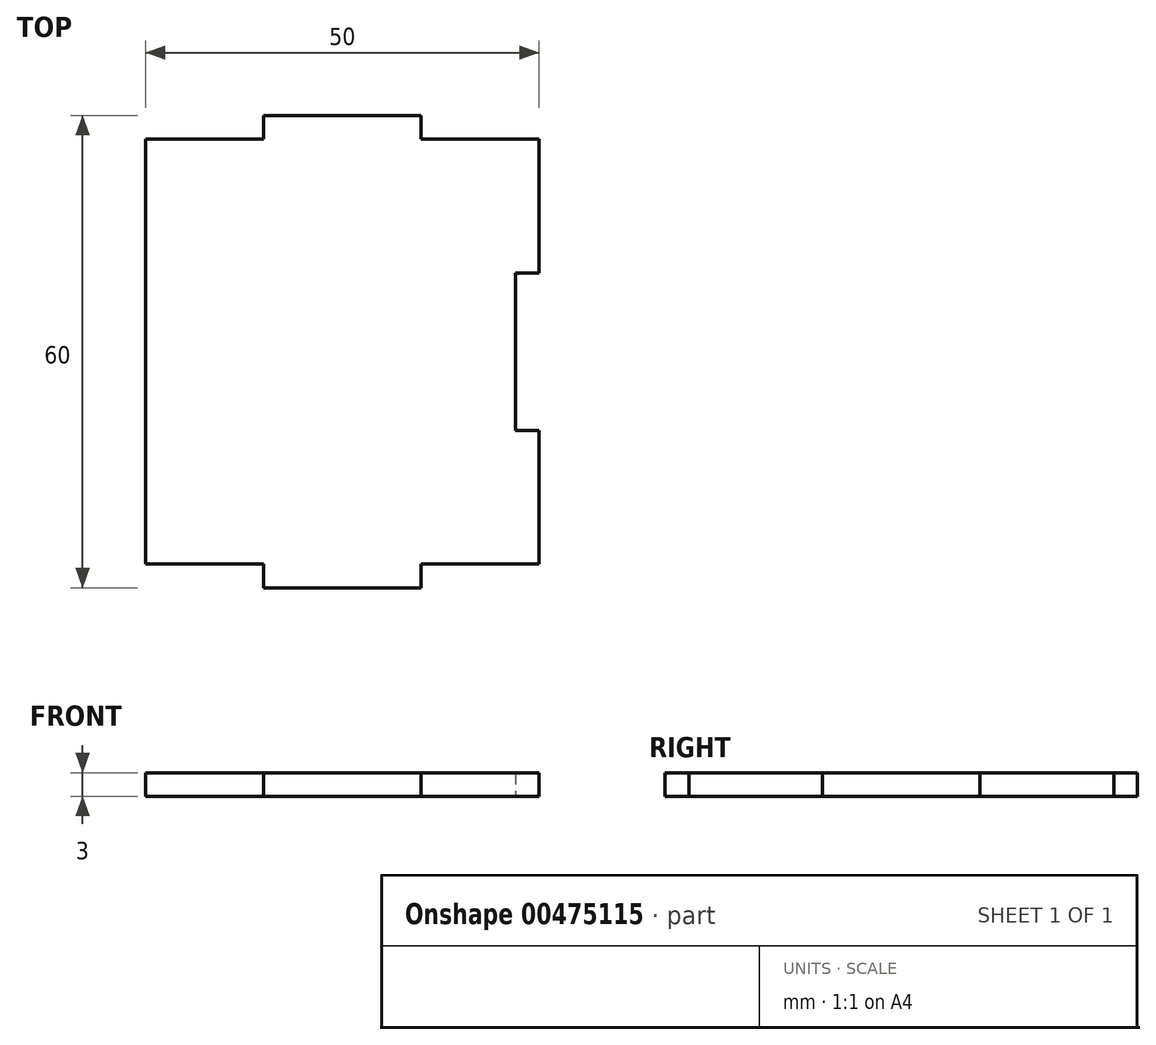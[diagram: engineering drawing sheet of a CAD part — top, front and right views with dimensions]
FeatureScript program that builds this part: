
annotation { "Feature Type Name" : "Feature", "Feature Type Description" : "" }
export const myFeature = defineFeature(function(context is Context, id is Id, definition is map)
    precondition{}
    {
        {
            var Q0;
            Q0=qCreatedBy(makeId("Top.planeOp"),FACE);
            var sketch = newSketch(context, id + "F0", { "sketchPlane" : qUnion([Q0])});
            skLineSegment(sketch, "E0.bottom", {"start": v(10, 30) * mm, "end": v(-10, 30) * mm});
            skLineSegment(sketch, "E0.top", {"start": v(10, -30) * mm, "end": v(-10, -30) * mm});
            skLineSegment(sketch, "E0.left", {"start": v(25, 27) * mm, "end": v(25, 10) * mm});
            skLineSegment(sketch, "E0.right", {"start": v(-25, 27) * mm, "end": v(-25, -27) * mm});
            skPoint(sketch, "E0.middle", {"position": v(0, 0) * mm});
            skLineSegment(sketch, "E1", {"start": v(-10, -30) * mm, "end": v(10, -30) * mm});
            skLineSegment(sketch, "E2", {"start": v(-10, -30) * mm, "end": v(-10, -27) * mm});
            skLineSegment(sketch, "E3", {"start": v(-10, -27) * mm, "end": v(-25, -27) * mm});
            skLineSegment(sketch, "E4", {"start": v(10, -30) * mm, "end": v(10, -27) * mm});
            skLineSegment(sketch, "E5", {"start": v(10, -27) * mm, "end": v(25, -27) * mm});
            skPoint(sketch, "E6.orphan", {"position": v(-25, -30) * mm});
            skPoint(sketch, "E7.orphan", {"position": v(25, -30) * mm});
            skLineSegment(sketch, "E8", {"start": v(-10, 30) * mm, "end": v(10, 30) * mm});
            skLineSegment(sketch, "E9", {"start": v(-10, 30) * mm, "end": v(-10, 27) * mm});
            skLineSegment(sketch, "E10", {"start": v(-10, 27) * mm, "end": v(-25, 27) * mm});
            skLineSegment(sketch, "E11", {"start": v(10, 30) * mm, "end": v(10, 27) * mm});
            skLineSegment(sketch, "E12", {"start": v(10, 27) * mm, "end": v(25, 27) * mm});
            skPoint(sketch, "E13.orphan", {"position": v(25, 30) * mm});
            skPoint(sketch, "E14.orphan", {"position": v(-25, 30) * mm});
            skLineSegment(sketch, "E15", {"start": v(25, -10) * mm, "end": v(25, -27) * mm});
            skLineSegment(sketch, "E16", {"start": v(25, 10) * mm, "end": v(22, 10) * mm});
            skLineSegment(sketch, "E17", {"start": v(22, 10) * mm, "end": v(22, -10) * mm});
            skLineSegment(sketch, "E18", {"start": v(25, -10) * mm, "end": v(22, -10) * mm});
            skSolve(sketch);
        }
        {
            var Q0;
            Q0=makeQuery(id+"F0.imprint","IMPRINT",FACE,{"disambiguationData":[TD([[makeQuery(id+"F0.imprint","IMPRINT",EDGE,{"derivedFrom":sQuery(id+"F0.wireOp",EDGE,"E0.right")}),1.0]])]});
            extrude(context, id + "F1", {"entities" : qUnion([Q0]), "depth" : 3 * mm});
        }
    });
